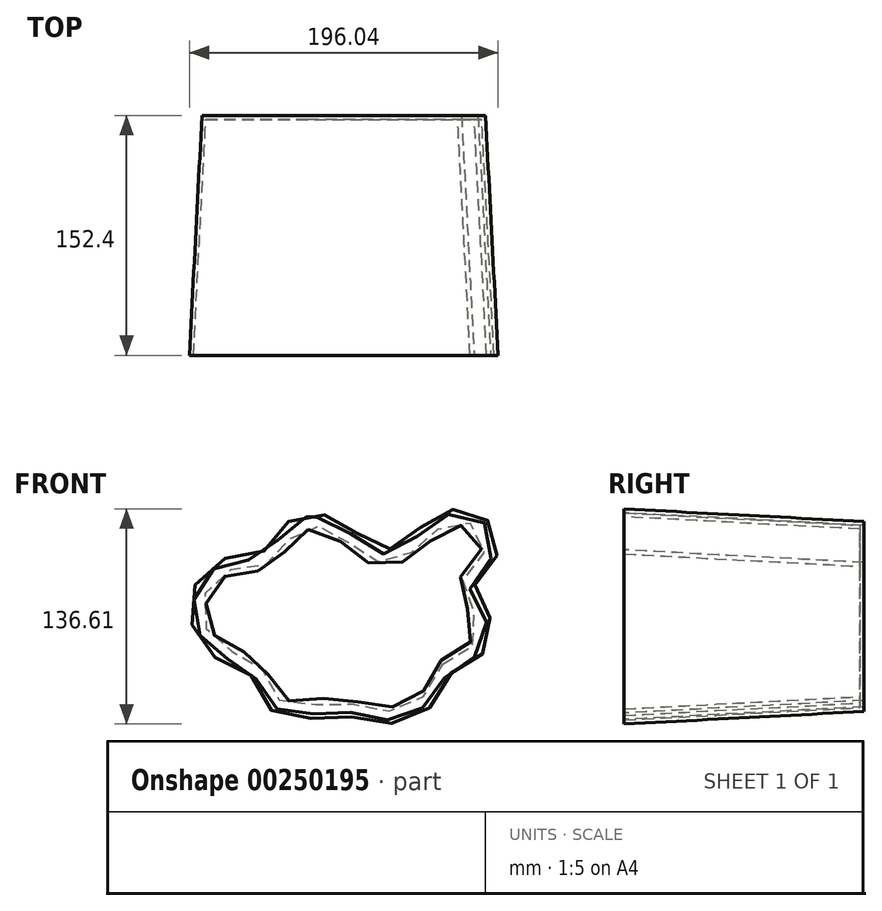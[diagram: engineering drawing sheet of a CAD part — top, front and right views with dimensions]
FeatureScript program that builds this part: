
annotation { "Feature Type Name" : "Feature", "Feature Type Description" : "" }
export const myFeature = defineFeature(function(context is Context, id is Id, definition is map)
    precondition{}
    {
        {
            var Q0;
            Q0=qCreatedBy(makeId("Front.planeOp"),FACE);
            var sketch = newSketch(context, id + "F0", { "sketchPlane" : qUnion([Q0])});
            skPoint(sketch, "E0.visualSharp", {"position": v(-76.34, 47.7) * mm});
            skPoint(sketch, "E1.visualSharp", {"position": v(76.06, 47.7) * mm});
            skPoint(sketch, "E2.visualSharp", {"position": v(76.06, -53.9) * mm});
            skPoint(sketch, "E3.visualSharp", {"position": v(-76.34, -53.9) * mm});
            skPoint(sketch, "E4.4.internal.snap0", {"position": v(-68.9, 40.26) * mm});
            skFitSpline(sketch, "E5", {"points": [v(-51.33, 26.77) * mm, v(-76.34, 22.3) * mm, v(-90.01, 10.73) * mm, v(-93.56, 0) * mm, v(-89.14, -18.26) * mm, v(-76.34, -28.5) * mm, v(-56.75, -38.2) * mm, v(-50.94, -53.9) * mm, v(-30.3, -64.36) * mm, v(-7.97, -60.3) * mm, v(20.15, -67.25) * mm, v(50.66, -53.9) * mm, v(59.34, -37.05) * mm, v(76.06, -28.5) * mm, v(80.73, -7.25) * mm, v(71.64, 8.07) * mm, v(76.06, 22.3) * mm, v(86.24, 35.08) * mm, v(78.7, 51.31) * mm, v(58.2, 49.73) * mm, v(40.38, 34.22) * mm, v(18.16, 27.6) * mm, v(0, 39.57) * mm, v(-29.23, 50.05) * mm, v(-51.33, 26.77) * mm]});
            skSolve(sketch);
        }
        {
            var Q0;
            Q0=makeQuery(id+"F0.imprint","IMPRINT",FACE,{"disambiguationData":[TD([[makeQuery(id+"F0.imprint","IMPRINT",EDGE,{"derivedFrom":sQuery(id+"F0.wireOp",EDGE,"E5")}),1.0]])]});
            extrude(context, id + "F1", {"entities" : qUnion([Q0]), "depth" : 152.4 * mm, "hasDraft" : true, "draftAngle" : 3 * degree});
        }
        {
            var Q0;
            Q0=makeQuery(id+"F1.opExtrude","CAP_FACE",FACE,{"disambiguationData":[OSD([sQuery(id+"F0.wireOp",EDGE,"E5")])],"isStart":false});
            shell(context, id + "F2", {"entities" : qUnion([Q0]), "thickness" : 2.54 * mm});
        }
    });
